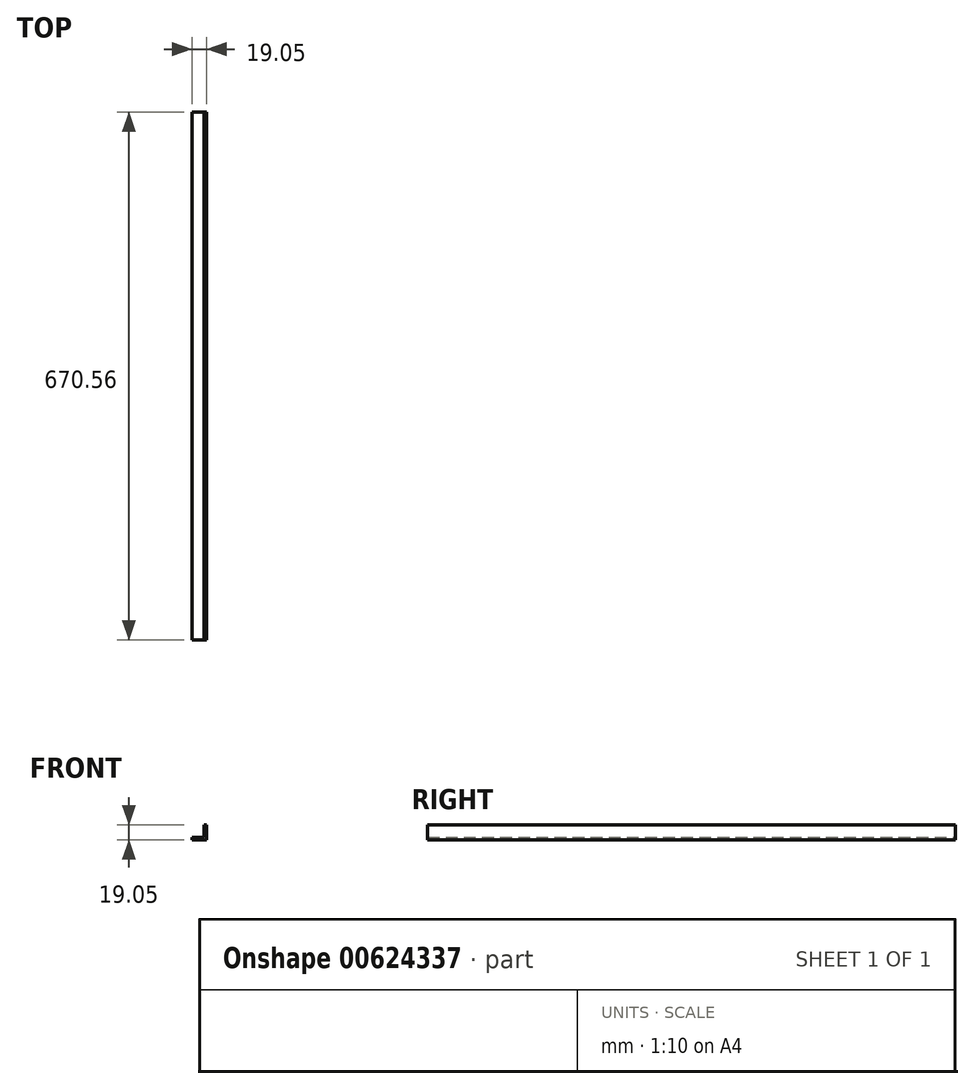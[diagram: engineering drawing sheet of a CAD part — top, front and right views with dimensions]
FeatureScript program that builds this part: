
annotation { "Feature Type Name" : "Feature", "Feature Type Description" : "" }
export const myFeature = defineFeature(function(context is Context, id is Id, definition is map)
    precondition{}
    {
        {
            var Q0;
            Q0=qCreatedBy(makeId("Front.planeOp"),FACE);
            var sketch = newSketch(context, id + "F0", { "sketchPlane" : qUnion([Q0])});
            skLineSegment(sketch, "E0", {"start": v(0, 0) * mm, "end": v(0, 19.05) * mm});
            skLineSegment(sketch, "E1", {"start": v(0, 19.05) * mm, "end": v(-3.25, 19.05) * mm});
            skLineSegment(sketch, "E2", {"start": v(-3.25, 19.05) * mm, "end": v(-3.25, 3.25) * mm});
            skLineSegment(sketch, "E3", {"start": v(-3.25, 3.25) * mm, "end": v(-19.05, 3.25) * mm});
            skLineSegment(sketch, "E4", {"start": v(-19.05, 3.25) * mm, "end": v(-19.05, 0) * mm});
            skLineSegment(sketch, "E5", {"start": v(-19.05, 0) * mm, "end": v(0, 0) * mm});
            skSolve(sketch);
        }
        {
            var Q0;
            Q0=makeQuery(id+"F0.imprint","IMPRINT",FACE,{"disambiguationData":[TD([[makeQuery(id+"F0.imprint","IMPRINT",EDGE,{"derivedFrom":sQuery(id+"F0.wireOp",EDGE,"E0")}),1.0]])]});
            extrude(context, id + "F1", {"entities" : qUnion([Q0]), "endBound" : BoundingType.SYMMETRIC, "depth" : 670.56 * mm, "offsetDistance" : 25.4 * mm});
        }
    });
